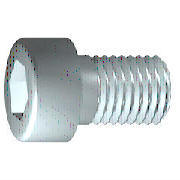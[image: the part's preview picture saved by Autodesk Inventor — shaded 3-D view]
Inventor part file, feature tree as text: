
AUTODESK INVENTOR PART (.ipt)
format: ipt  version: 2024 (Build 280153000, 153)  size: 186,880 bytes
history: native  units: mm (DEFAULTED — no unit token found)
features: fillet x2, sketch x2, extrude x1, thread x1, chamfer x1, plane x1
ambient origin geometry x7: Origin, YZ Plane, XY Plane, X Axis, Y Axis, Z Axis, Center Point
bodies: Solid1 (feature_tree), Body (feature_tree)
feature tree (8):
  extrude  "Slot"  Depth=2.0mm
  fillet  "Fillet1"  Radius=4.0mm
  thread  "Thread"  [1 undecoded]
  chamfer  "Chamfer1"  Distance=4.0mm
  plane  "Work Plane1"
  fillet  "Fillet2"  Radius=4.0mm
  sketch  "Sketch1"  dims[d1=23.25mm d2=0.429515mm d3=4.0mm d4=2.0mm]
  sketch  "Sketch2"  dims[d5=60.0deg d6=4.0mm d7=4.0mm d8=3.464102mm d9=7.0mm d10=90.0deg d11=10.0mm d12=0.0mm d13=23.25mm d14=0.0mm d15=0.429415mm d16=0.429415mm d17=0.4mm d19=0.0mm d26=25.0mm d27=45.0deg d28=0.0mm d29=0.0mm d30=0.1mm]
note: 1 required parameter value undecoded (feature->parameter linkage not recoverable at this tier; creation-order binding heuristic only, values carry confidence <= 0.55)
